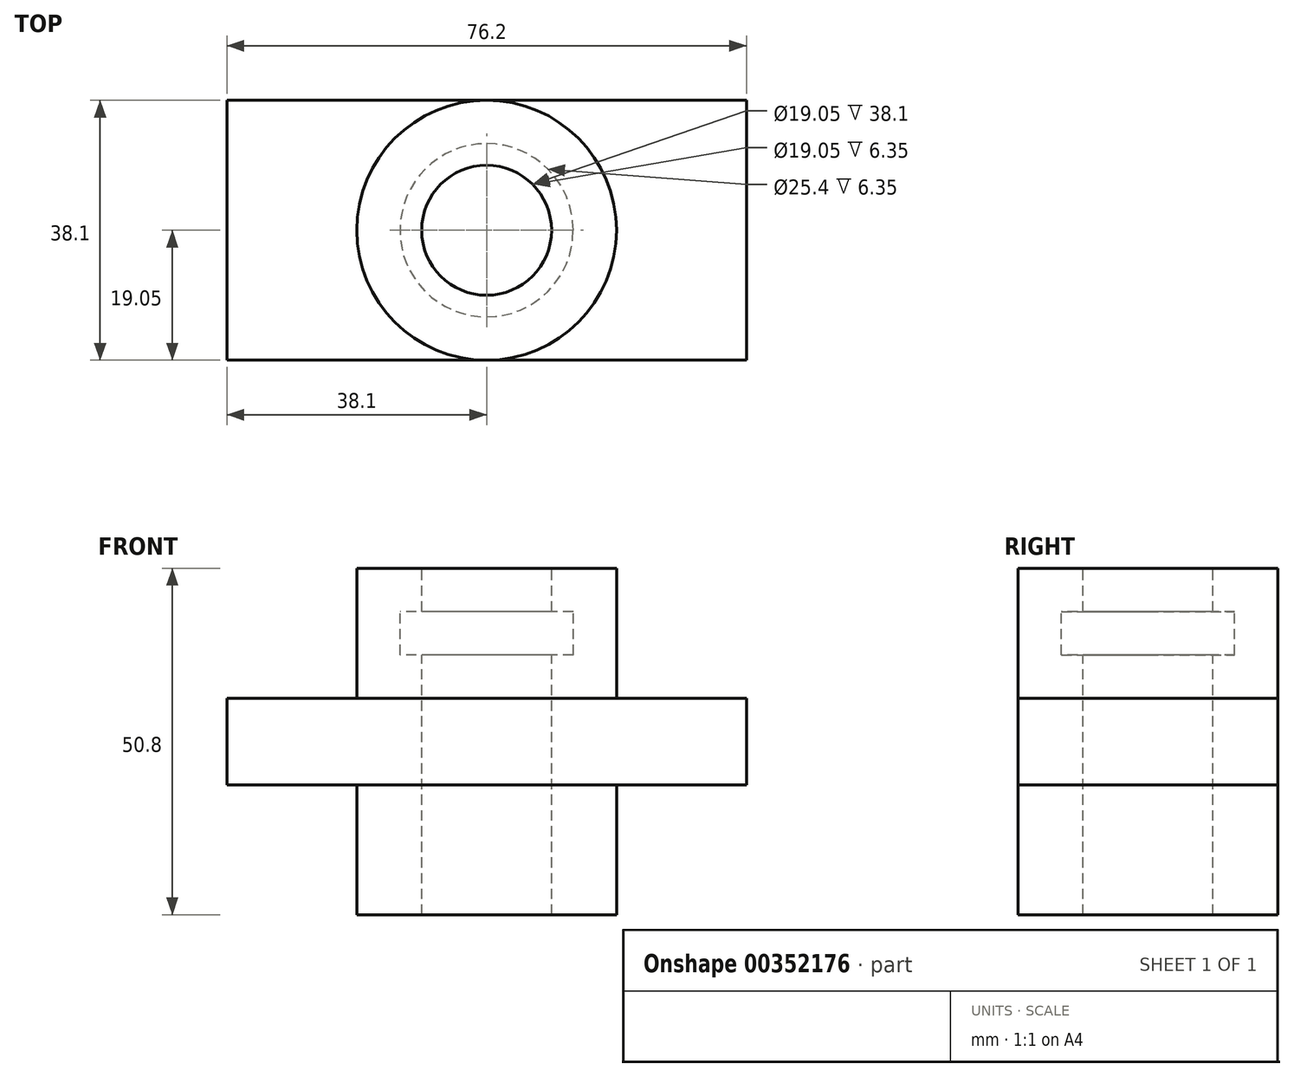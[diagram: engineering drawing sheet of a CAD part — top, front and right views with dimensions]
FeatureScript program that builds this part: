
annotation { "Feature Type Name" : "Feature", "Feature Type Description" : "" }
export const myFeature = defineFeature(function(context is Context, id is Id, definition is map)
    precondition{}
    {
        {
            var Q0;
            Q0=qCreatedBy(makeId("Top.planeOp"),FACE);
            var sketch = newSketch(context, id + "F0", { "sketchPlane" : qUnion([Q0])});
            skLineSegment(sketch, "E0.bottom", {"start": v(38.1, 19.05) * mm, "end": v(-38.1, 19.05) * mm});
            skLineSegment(sketch, "E0.top", {"start": v(38.1, -19.05) * mm, "end": v(-38.1, -19.05) * mm});
            skLineSegment(sketch, "E0.left", {"start": v(38.1, 19.05) * mm, "end": v(38.1, -19.05) * mm});
            skLineSegment(sketch, "E0.right", {"start": v(-38.1, 19.05) * mm, "end": v(-38.1, -19.05) * mm});
            skPoint(sketch, "E0.middle", {"position": v(0, 0) * mm});
            skCircle(sketch, "E1", {"center": v(0, 0) * mm, "radius": 19.05 * mm});
            skSolve(sketch);
        }
        {
            var Q0;
            {var subQ0=sQuery(id+"F0.wireOp",EDGE,"E0.right");Q0=makeQuery(id+"F0.imprint","IMPRINT",FACE,{"disambiguationData":[TD([[makeQuery(id+"F0.imprint","IMPRINT",EDGE,{"derivedFrom":subQ0}),1.0]])]});}
            var Q1;
            {var subQ0=sQuery(id+"F0.wireOp",EDGE,"E0.left");Q1=makeQuery(id+"F0.imprint","IMPRINT",FACE,{"disambiguationData":[TD([[makeQuery(id+"F0.imprint","IMPRINT",EDGE,{"derivedFrom":subQ0}),-1.0]])]});}
            extrude(context, id + "F1", {"entities" : qUnion([Q0, Q1]), "depth" : 12.7 * mm, "symmetric" : true});
        }
        {
            var Q0;
            {var subQ0=sQuery(id+"F0.wireOp",EDGE,"E1");var subQ1=makeQuery(id+"F0.imprint","INTERSECT",VERTEX,{"derivedFrom":[sQuery(id+"F0.wireOp",EDGE,"E0.bottom"),subQ0]});Q0=makeQuery(id+"F0.imprint","IMPRINT",FACE,{"disambiguationData":[TD([[makeQuery(id+"F0.imprint","IMPRINT",EDGE,{"disambiguationData":[TD([[subQ1,-1.0]])],"derivedFrom":subQ0}),1.0]])]});}
            extrude(context, id + "F2", {"entities" : qUnion([Q0]), "operationType" : NewBodyOperationType.ADD, "depth" : 50.8 * mm, "symmetric" : true});
        }
        {
            var Q0;
            Q0=makeQuery(id+"F2.opExtrude","CAP_FACE",FACE,{"disambiguationData":[OSD([sQuery(id+"F0.wireOp",EDGE,"E1")])],"isStart":false});
            var sketch = newSketch(context, id + "F3", { "sketchPlane" : qUnion([Q0])});
            skCircle(sketch, "E2", {"center": v(0, 0) * mm, "radius": 9.53 * mm});
            skCircle(sketch, "E3", {"center": v(0, 0) * mm, "radius": 12.7 * mm});
            skSolve(sketch);
        }
        {
            var Q0;
            Q0=makeQuery(id+"F3.imprint","IMPRINT",FACE,{"disambiguationData":[TD([[makeQuery(id+"F3.imprint","IMPRINT",EDGE,{"derivedFrom":sQuery(id+"F3.wireOp",EDGE,"E2")}),1.0]])]});
            extrude(context, id + "F4", {"entities" : qUnion([Q0]), "operationType" : NewBodyOperationType.REMOVE, "endBound" : BoundingType.THROUGH_ALL, "oppositeDirection" : true, "depth" : 25.4 * mm});
        }
        {
            var Q0;
            Q0=makeQuery(id+"F3.imprint","IMPRINT",FACE,{"disambiguationData":[TD([[makeQuery(id+"F3.imprint","IMPRINT",EDGE,{"derivedFrom":sQuery(id+"F3.wireOp",EDGE,"E2")}),-1.0]])]});
            extrude(context, id + "F5", {"entities" : qUnion([Q0]), "operationType" : NewBodyOperationType.REMOVE, "oppositeDirection" : true, "depth" : 12.7 * mm, "hasSecondDirection" : true, "secondDirectionOppositeDirection" : true, "secondDirectionDepth" : 6.35 * mm});
        }
    });
